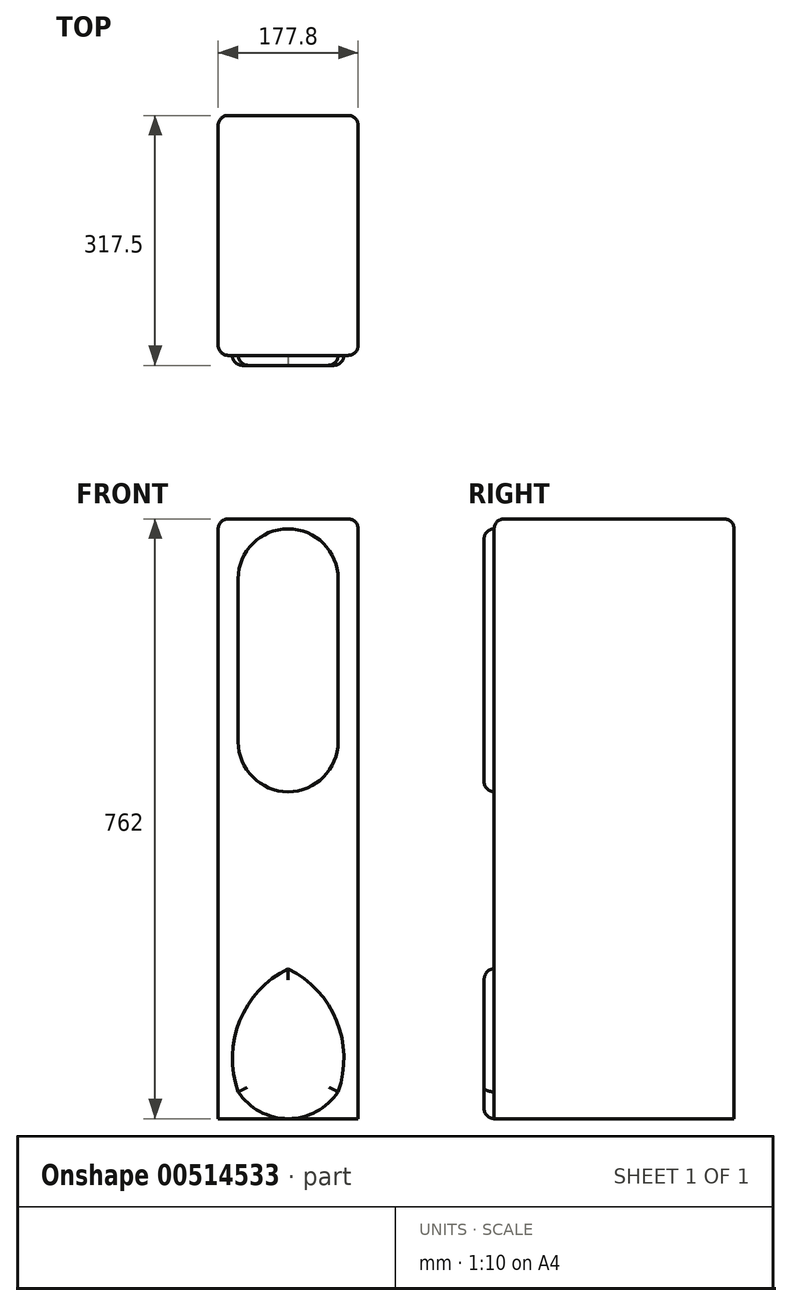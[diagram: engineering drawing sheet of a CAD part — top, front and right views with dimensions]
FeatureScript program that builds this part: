
annotation { "Feature Type Name" : "Feature", "Feature Type Description" : "" }
export const myFeature = defineFeature(function(context is Context, id is Id, definition is map)
    precondition{}
    {
        {
            var Q0;
            Q0=qCreatedBy(makeId("Top.planeOp"),FACE);
            var sketch = newSketch(context, id + "F0", { "sketchPlane" : qUnion([Q0])});
            skLineSegment(sketch, "E0.bottom", {"start": v(88.9, 152.4) * mm, "end": v(-88.9, 152.4) * mm});
            skLineSegment(sketch, "E0.top", {"start": v(88.9, -152.4) * mm, "end": v(-88.9, -152.4) * mm});
            skLineSegment(sketch, "E0.left", {"start": v(88.9, 152.4) * mm, "end": v(88.9, -152.4) * mm});
            skLineSegment(sketch, "E0.right", {"start": v(-88.9, 152.4) * mm, "end": v(-88.9, -152.4) * mm});
            skPoint(sketch, "E0.middle", {"position": v(0, 0) * mm});
            skSolve(sketch);
        }
        {
            var Q0;
            Q0=makeQuery(id+"F0.imprint","IMPRINT",FACE,{"disambiguationData":[TD([[makeQuery(id+"F0.imprint","IMPRINT",EDGE,{"derivedFrom":sQuery(id+"F0.wireOp",EDGE,"E0.bottom")}),1.0]])]});
            extrude(context, id + "F1", {"entities" : qUnion([Q0]), "depth" : 762 * mm, "offsetDistance" : 25.4 * mm});
        }
        {
            var Q0;
            Q0=makeQuery(id+"F1.opExtrude","SWEPT_FACE",FACE,{"disambiguationData":[OSD([sQuery(id+"F0.wireOp",EDGE,"E0.top")])]});
            var sketch = newSketch(context, id + "F2", { "sketchPlane" : qUnion([Q0])});
            skArc(sketch, "E1", {"start": v(-63.5, 34.08) * mm, "mid": v(0, 0) * mm, "end": v(63.5, 34.08) * mm});
            skArc(sketch, "E2", {"start": v(0, 190.5) * mm, "mid": v(-61.5, 124.37) * mm, "end": v(-63.5, 34.08) * mm});
            skArc(sketch, "E3", {"start": v(63.5, 34.08) * mm, "mid": v(61.5, 124.37) * mm, "end": v(0, 190.5) * mm});
            skLineSegment(sketch, "E4", {"start": v(-63.5, 685.8) * mm, "end": v(-63.5, 478.8) * mm});
            skLineSegment(sketch, "E5", {"start": v(63.5, 685.8) * mm, "end": v(63.5, 478.8) * mm});
            skArc(sketch, "E6", {"start": v(63.5, 685.8) * mm, "mid": v(0, 749.3) * mm, "end": v(-63.5, 685.8) * mm});
            skArc(sketch, "E7", {"start": v(-63.5, 478.8) * mm, "mid": v(0, 415.3) * mm, "end": v(63.5, 478.8) * mm});
            skSolve(sketch);
        }
        {
            var Q0;
            {var subQ0=sQuery(id+"F2.wireOp",EDGE,"E2");Q0=makeQuery(id+"F2.imprint","IMPRINT",FACE,{"disambiguationData":[TD([[makeQuery(id+"F2.imprint","IMPRINT",EDGE,{"derivedFrom":subQ0}),1.0]])]});}
            var Q1;
            Q1=makeQuery(id+"F2.imprint","IMPRINT",FACE,{"disambiguationData":[TD([[makeQuery(id+"F2.imprint","IMPRINT",EDGE,{"derivedFrom":sQuery(id+"F2.wireOp",EDGE,"E4")}),1.0]])]});
            extrude(context, id + "F3", {"entities" : qUnion([Q0, Q1]), "operationType" : NewBodyOperationType.ADD, "depth" : 12.7 * mm, "offsetDistance" : 25.4 * mm});
        }
        {
            var Q0;
            Q0=makeQuery(id+"F3.opExtrude","CAP_FACE",FACE,{"disambiguationData":[OSD([sQuery(id+"F2.wireOp",EDGE,"E4"),sQuery(id+"F2.wireOp",EDGE,"E5"),sQuery(id+"F2.wireOp",EDGE,"E6"),sQuery(id+"F2.wireOp",EDGE,"E7")])],"isStart":false});
            var Q1;
            Q1=makeQuery(id+"F3.opExtrude","CAP_FACE",FACE,{"disambiguationData":[OSD([sQuery(id+"F2.wireOp",EDGE,"E1"),sQuery(id+"F2.wireOp",EDGE,"E2"),sQuery(id+"F2.wireOp",EDGE,"E3")])],"isStart":false});
            fillet(context, id + "F4", {"entities" : qUnion([Q0, Q1]), "radius" : 12.7 * mm, "tangentPropagation" : true, "allowEdgeOverflow" : false});
        }
        {
            var Q0;
            Q0=makeQuery(id+"F1.opExtrude","CAP_FACE",FACE,{"disambiguationData":[OSD([sQuery(id+"F0.wireOp",EDGE,"E0.bottom"),sQuery(id+"F0.wireOp",EDGE,"E0.top"),sQuery(id+"F0.wireOp",EDGE,"E0.left"),sQuery(id+"F0.wireOp",EDGE,"E0.right")])],"isStart":false});
            var Q1;
            Q1=makeQuery(id+"F1.opExtrude","SWEPT_EDGE",EDGE,{"disambiguationData":[OSD([sQuery(id+"F0.wireOp",EDGE,"E0.top"),sQuery(id+"F0.wireOp",EDGE,"E0.right")])]});
            var Q2;
            Q2=makeQuery(id+"F1.opExtrude","SWEPT_EDGE",EDGE,{"disambiguationData":[OSD([sQuery(id+"F0.wireOp",EDGE,"E0.bottom"),sQuery(id+"F0.wireOp",EDGE,"E0.right")])]});
            var Q3;
            Q3=makeQuery(id+"F1.opExtrude","SWEPT_EDGE",EDGE,{"disambiguationData":[OSD([sQuery(id+"F0.wireOp",EDGE,"E0.top"),sQuery(id+"F0.wireOp",EDGE,"E0.left")])]});
            var Q4;
            Q4=makeQuery(id+"F1.opExtrude","SWEPT_EDGE",EDGE,{"disambiguationData":[OSD([sQuery(id+"F0.wireOp",EDGE,"E0.bottom"),sQuery(id+"F0.wireOp",EDGE,"E0.left")])]});
            fillet(context, id + "F5", {"entities" : qUnion([Q0, Q1, Q2, Q3, Q4]), "radius" : 12.7 * mm, "tangentPropagation" : true, "allowEdgeOverflow" : false});
        }
    });
